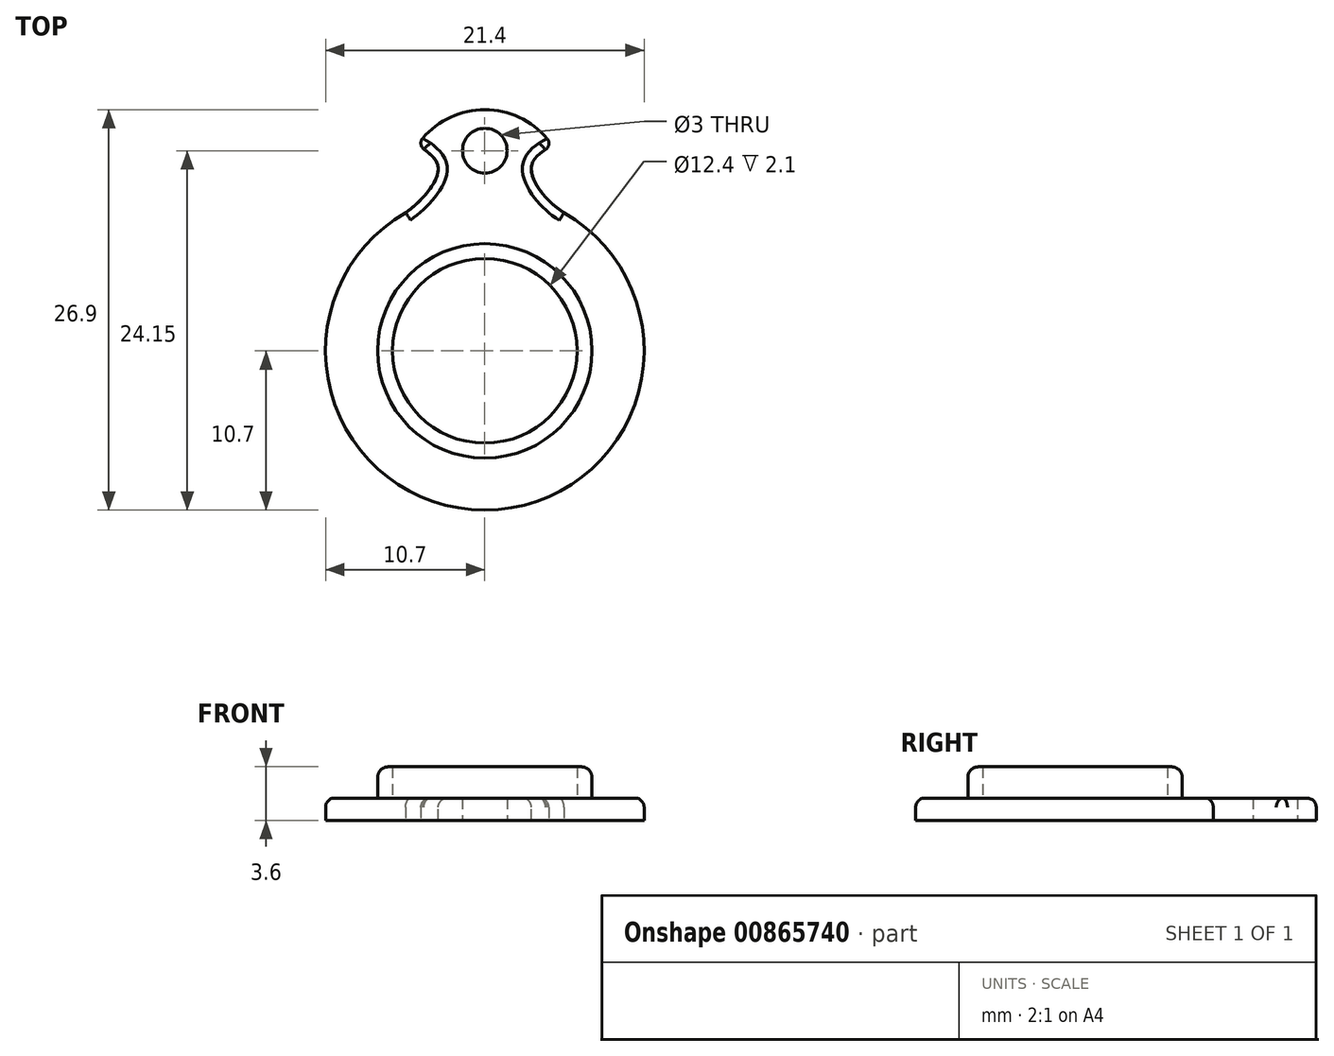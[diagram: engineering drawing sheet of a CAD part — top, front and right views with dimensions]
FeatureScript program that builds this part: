
annotation { "Feature Type Name" : "Feature", "Feature Type Description" : "" }
export const myFeature = defineFeature(function(context is Context, id is Id, definition is map)
    precondition{}
    {
        {
            var Q0;
            Q0=qCreatedBy(makeId("Top.planeOp"),FACE);
            var sketch = newSketch(context, id + "F0", { "sketchPlane" : qUnion([Q0])});
            skCircle(sketch, "E0", {"center": v(0, 0) * mm, "radius": 10.7 * mm});
            skCircle(sketch, "E1", {"center": v(0, 0) * mm, "radius": 6.2 * mm});
            skCircle(sketch, "E2", {"center": v(0, 0) * mm, "radius": 7.2 * mm});
            skArc(sketch, "E3", {"start": v(5.32, 9.29) * mm, "mid": v(0, 16.2) * mm, "end": v(-5.32, 9.29) * mm});
            skLineSegment(sketch, "E4", {"start": v(0, 16.2) * mm, "end": v(0, 10.7) * mm, "construction": true});
            skCircle(sketch, "E5", {"center": v(0, 13.45) * mm, "radius": 1.5 * mm});
            skFitSpline(sketch, "E6", {"points": [v(-4.51, 13.85) * mm, v(-3.13, 12.28) * mm, v(-5.32, 9.29) * mm], "startDerivative": vector(5.07, -3.58) * mm, "endDerivative": vector(-6.25, -4.47) * mm});
            skFitSpline(sketch, "E7", {"points": [v(4.54, 13.8) * mm, v(3.13, 12.28) * mm, v(5.32, 9.29) * mm], "startDerivative": vector(-5.92, -3.45) * mm, "endDerivative": vector(7.02, -4.52) * mm});
            skSolve(sketch);
        }
        {
            var Q0;
            Q0=makeQuery(id+"F0.imprint","IMPRINT",FACE,{"disambiguationData":[TD([[makeQuery(id+"F0.imprint","IMPRINT",EDGE,{"derivedFrom":sQuery(id+"F0.wireOp",EDGE,"E2")}),-1.0]])]});
            var Q1;
            Q1=makeQuery(id+"F0.imprint","IMPRINT",FACE,{"disambiguationData":[TD([[makeQuery(id+"F0.imprint","IMPRINT",EDGE,{"derivedFrom":sQuery(id+"F0.wireOp",EDGE,"E1")}),1.0]])]});
            var Q2;
            Q2=makeQuery(id+"F0.imprint","IMPRINT",FACE,{"disambiguationData":[TD([[makeQuery(id+"F0.imprint","IMPRINT",EDGE,{"derivedFrom":sQuery(id+"F0.wireOp",EDGE,"E5")}),-1.0]])]});
            extrude(context, id + "F1", {"entities" : qUnion([Q0, Q1, Q2]), "depth" : 1.5 * mm, "offsetDistance" : 25 * mm});
        }
        {
            var Q0;
            Q0=makeQuery(id+"F0.imprint","IMPRINT",FACE,{"disambiguationData":[TD([[makeQuery(id+"F0.imprint","IMPRINT",EDGE,{"derivedFrom":sQuery(id+"F0.wireOp",EDGE,"E5")}),1.0]])]});
            extrude(context, id + "F2", {"entities" : qUnion([Q0]), "operationType" : NewBodyOperationType.REMOVE, "oppositeDirection" : true, "depth" : 3 * mm, "offsetDistance" : 25 * mm});
        }
        {
            var Q0;
            Q0=makeQuery(id+"F0.imprint","IMPRINT",FACE,{"disambiguationData":[TD([[makeQuery(id+"F0.imprint","IMPRINT",EDGE,{"derivedFrom":sQuery(id+"F0.wireOp",EDGE,"E1")}),-1.0]])]});
            extrude(context, id + "F3", {"entities" : qUnion([Q0]), "operationType" : NewBodyOperationType.ADD, "depth" : 3.6 * mm, "offsetDistance" : 25 * mm});
        }
        {
            var Q0;
            Q0=makeQuery(id+"F3.opExtrude","CAP_EDGE",EDGE,{"disambiguationData":[OSD([sQuery(id+"F0.wireOp",EDGE,"E2")])],"isStart":false});
            fillet(context, id + "F4", {"entities" : qUnion([Q0]), "radius" : 0.7 * mm, "tangentPropagation" : true, "allowEdgeOverflow" : false});
        }
        {
            var Q0;
            Q0=makeQuery(id+"F1.opExtrude","CAP_EDGE",EDGE,{"disambiguationData":[OSD([sQuery(id+"F0.wireOp",EDGE,"E6")])],"isStart":false});
            var Q1;
            Q1=makeQuery(id+"F1.opExtrude","CAP_EDGE",EDGE,{"disambiguationData":[OSD([sQuery(id+"F0.wireOp",EDGE,"E3")])],"isStart":false});
            var Q2;
            Q2=makeQuery(id+"F1.opExtrude","CAP_EDGE",EDGE,{"disambiguationData":[OSD([sQuery(id+"F0.wireOp",EDGE,"E7")])],"isStart":false});
            var Q3;
            Q3=makeQuery(id+"F1.opExtrude","CAP_EDGE",EDGE,{"disambiguationData":[OSD([sQuery(id+"F0.wireOp",EDGE,"E0")])],"isStart":false});
            var Q4;
            Q4=makeQuery(id+"F1.opExtrude","CAP_EDGE",EDGE,{"disambiguationData":[OSD([sQuery(id+"F0.wireOp",EDGE,"E2")])],"isStart":false});
            fillet(context, id + "F5", {"entities" : qUnion([Q0, Q1, Q2, Q3, Q4]), "radius" : 0.6 * mm, "tangentPropagation" : true, "allowEdgeOverflow" : false});
        }
        {
            var Q0;
            Q0=makeQuery(id+"F1.opExtrude","SWEPT_EDGE",EDGE,{"disambiguationData":[OSD([sQuery(id+"F0.wireOp",EDGE,"E3"),sQuery(id+"F0.wireOp",EDGE,"E6")])]});
            var Q1;
            Q1=makeQuery(id+"F1.opExtrude","SWEPT_EDGE",EDGE,{"disambiguationData":[OSD([sQuery(id+"F0.wireOp",EDGE,"E3"),sQuery(id+"F0.wireOp",EDGE,"E7")])]});
            fillet(context, id + "F6", {"entities" : qUnion([Q0, Q1]), "radius" : 0.5 * mm, "tangentPropagation" : true, "allowEdgeOverflow" : false});
        }
    });
